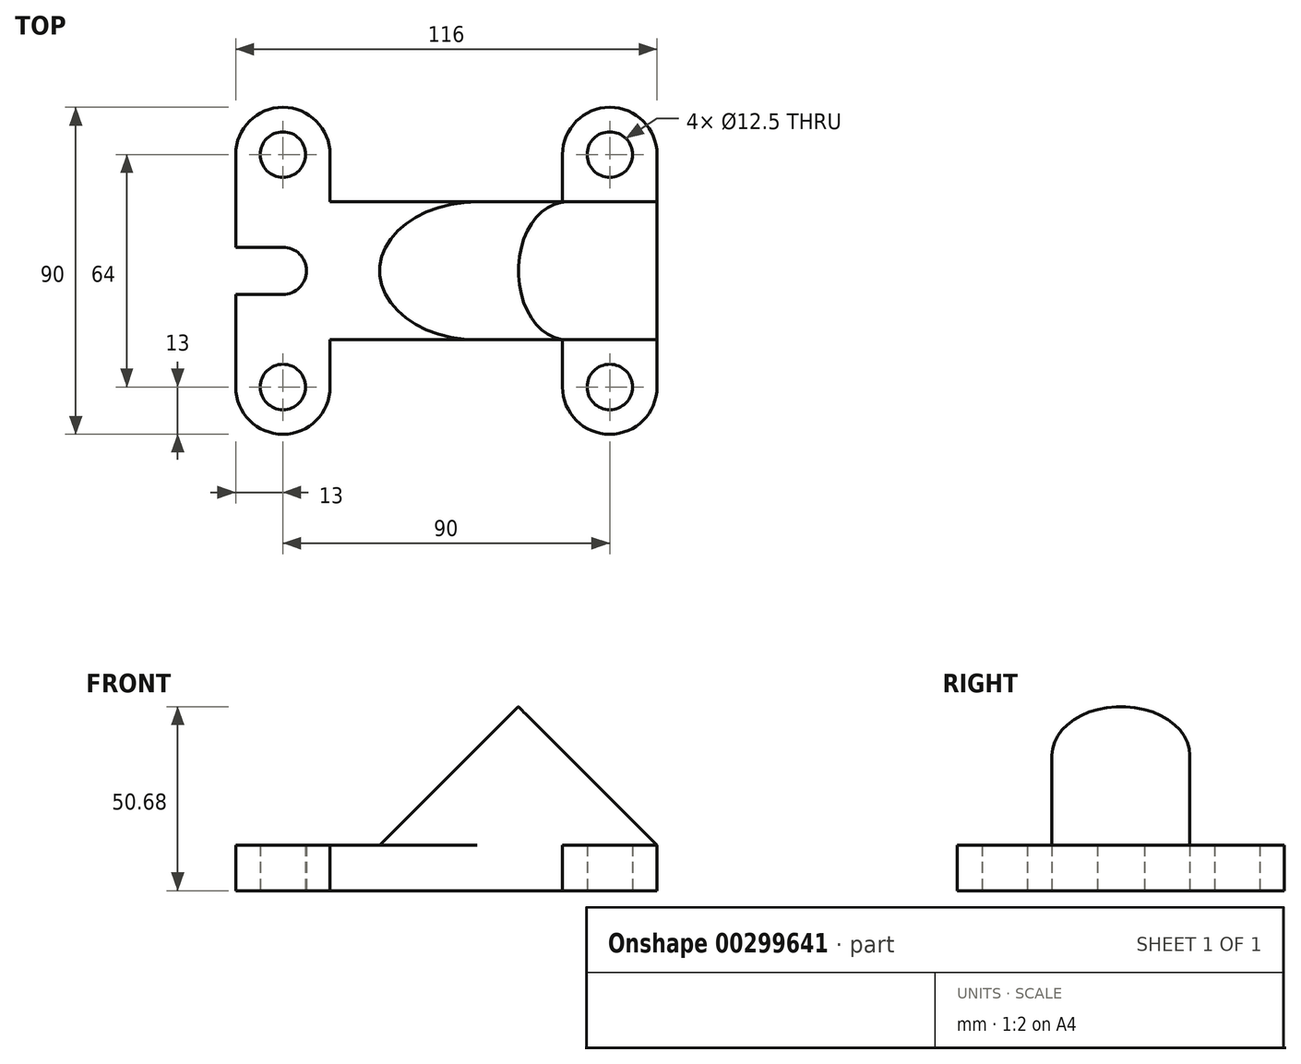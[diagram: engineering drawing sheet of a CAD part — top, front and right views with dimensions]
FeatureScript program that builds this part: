
annotation { "Feature Type Name" : "Feature", "Feature Type Description" : "" }
export const myFeature = defineFeature(function(context is Context, id is Id, definition is map)
    precondition{}
    {
        {
            var Q0;
            Q0=qCreatedBy(makeId("Top.planeOp"),FACE);
            var sketch = newSketch(context, id + "F0", { "sketchPlane" : qUnion([Q0])});
            skArc(sketch, "E0", {"start": v(-13, 0) * mm, "mid": v(0, -13) * mm, "end": v(13, 0) * mm});
            skArc(sketch, "E1.0.1.0", {"start": v(13, 64) * mm, "mid": v(0, 77) * mm, "end": v(-13, 64) * mm});
            skArc(sketch, "E1.1.0.0", {"start": v(77, 0) * mm, "mid": v(90, -13) * mm, "end": v(103, 0) * mm});
            skArc(sketch, "E1.1.1.0", {"start": v(103, 64) * mm, "mid": v(90, 77) * mm, "end": v(77, 64) * mm});
            skLineSegment(sketch, "E1.direction1", {"start": v(0, 0) * mm, "end": v(90, 0) * mm, "construction": true});
            skLineSegment(sketch, "E1.direction2", {"start": v(0, 0) * mm, "end": v(0, 64) * mm, "construction": true});
            skLineSegment(sketch, "E2", {"start": v(103, 0) * mm, "end": v(103, 64) * mm});
            skLineSegment(sketch, "E3", {"start": v(-13, 0) * mm, "end": v(-13, 25.5) * mm});
            skArc(sketch, "E4", {"start": v(0, 25.5) * mm, "mid": v(6.5, 32) * mm, "end": v(0, 38.5) * mm});
            skLineSegment(sketch, "E5", {"start": v(0, 38.5) * mm, "end": v(-13, 38.5) * mm});
            skLineSegment(sketch, "E6", {"start": v(0, 25.5) * mm, "end": v(-13, 25.5) * mm});
            skLineSegment(sketch, "E7", {"start": v(0, 32) * mm, "end": v(90, 32) * mm, "construction": true});
            skLineSegment(sketch, "E8.0", {"start": v(13, 13) * mm, "end": v(77, 13) * mm});
            skLineSegment(sketch, "E9.0", {"start": v(13, 51) * mm, "end": v(77, 51) * mm});
            skLineSegment(sketch, "E10", {"start": v(13, 64) * mm, "end": v(13, 51) * mm});
            skLineSegment(sketch, "E11", {"start": v(77, 64) * mm, "end": v(77, 51) * mm});
            skLineSegment(sketch, "E12", {"start": v(77, 0) * mm, "end": v(77, 13) * mm});
            skLineSegment(sketch, "E13", {"start": v(13, 0) * mm, "end": v(13, 13) * mm});
            skLineSegment(sketch, "E14.trimOffspring", {"start": v(-13, 38.5) * mm, "end": v(-13, 64) * mm});
            skCircle(sketch, "E15", {"center": v(0, 64) * mm, "radius": 6.25 * mm});
            skCircle(sketch, "E16", {"center": v(0, 0) * mm, "radius": 6.25 * mm});
            skCircle(sketch, "E17", {"center": v(90, 0) * mm, "radius": 6.25 * mm});
            skCircle(sketch, "E18", {"center": v(90, 64) * mm, "radius": 6.25 * mm});
            skSolve(sketch);
        }
        {
            var Q0;
            Q0=makeQuery(id+"F0.imprint","IMPRINT",FACE,{"disambiguationData":[TD([[makeQuery(id+"F0.imprint","IMPRINT",EDGE,{"derivedFrom":sQuery(id+"F0.wireOp",EDGE,"E0")}),1.0]])]});
            extrude(context, id + "F1", {"entities" : qUnion([Q0]), "depth" : 12.5 * mm});
        }
        {
            var Q0;
            Q0=makeQuery(id+"F1.opExtrude","SWEPT_FACE",FACE,{"disambiguationData":[OSD([sQuery(id+"F0.wireOp",EDGE,"E8.0")])]});
            var sketch = newSketch(context, id + "F2", { "sketchPlane" : qUnion([Q0])});
            skLineSegment(sketch, "E19.0", {"start": v(77, 12.5) * mm, "end": v(103, 12.5) * mm});
            skLineSegment(sketch, "E20", {"start": v(103, 12.5) * mm, "end": v(64.82, 50.68) * mm});
            skLineSegment(sketch, "E21", {"start": v(64.82, 50.68) * mm, "end": v(26.63, 12.5) * mm});
            skSolve(sketch);
        }
        {
            var Q0;
            {var subQ0=sQuery(id+"F2.wireOp",EDGE,"E19.0");Q0=makeQuery(id+"F2.imprint","IMPRINT",FACE,{"disambiguationData":[TD([[makeQuery(id+"F2.imprint","IMPRINT",EDGE,{"derivedFrom":subQ0}),1.0]])]});}
            extrude(context, id + "F3", {"entities" : qUnion([Q0]), "operationType" : NewBodyOperationType.ADD, "oppositeDirection" : true, "depth" : (19 * 2) * mm});
        }
        {
            var Q0;
            Q0=makeQuery(id+"F3.opExtrude","CAP_EDGE",EDGE,{"disambiguationData":[OSD([sQuery(id+"F2.wireOp",EDGE,"E21")])],"isStart":true});
            var Q1;
            Q1=makeQuery(id+"F3.opExtrude","CAP_EDGE",EDGE,{"disambiguationData":[OSD([sQuery(id+"F2.wireOp",EDGE,"E21")])],"isStart":false});
            fillet(context, id + "F4", {"entities" : qUnion([Q0, Q1]), "radius" : 19 * mm, "tangentPropagation" : true, "allowEdgeOverflow" : false});
        }
        {
            var Q0;
            Q0=makeQuery(id+"F3.opExtrude","SWEPT_FACE",FACE,{"disambiguationData":[OSD([sQuery(id+"F2.wireOp",EDGE,"E20")])]});
            var sketch = newSketch(context, id + "F5", { "sketchPlane" : qUnion([Q0])});
            skArc(sketch, "E22.0", {"start": v(29, 51) * mm, "mid": v(10, 32) * mm, "end": v(29, 13) * mm});
            skCircle(sketch, "E23", {"center": v(29, 32) * mm, "radius": 12.5 * mm, "construction": true});
            skCircle(sketch, "E24", {"center": v(16.5, 32) * mm, "radius": 2.5 * mm});
            skPoint(sketch, "E25.center", {"position": v(0, 0) * mm});
            skCircle(sketch, "E26.1.0", {"center": v(25.13, 20.11) * mm, "radius": 2.5 * mm});
            skCircle(sketch, "E26.2.0", {"center": v(39.1, 24.65) * mm, "radius": 2.5 * mm});
            skCircle(sketch, "E26.3.0", {"center": v(39.1, 39.35) * mm, "radius": 2.5 * mm});
            skCircle(sketch, "E26.4.0", {"center": v(25.13, 43.89) * mm, "radius": 2.5 * mm});
            skSolve(sketch);
        }
        {
            var Q0;
            Q0=makeQuery(id+"F5.imprint","IMPRINT",FACE,{"disambiguationData":[TD([[makeQuery(id+"F5.imprint","IMPRINT",EDGE,{"derivedFrom":sQuery(id+"F5.wireOp",EDGE,"E26.1.0")}),1.0]])]});
            var Q1;
            Q1=makeQuery(id+"F5.imprint","IMPRINT",FACE,{"disambiguationData":[TD([[makeQuery(id+"F5.imprint","IMPRINT",EDGE,{"derivedFrom":sQuery(id+"F5.wireOp",EDGE,"E26.2.0")}),1.0]])]});
            var Q2;
            Q2=makeQuery(id+"F5.imprint","IMPRINT",FACE,{"disambiguationData":[TD([[makeQuery(id+"F5.imprint","IMPRINT",EDGE,{"derivedFrom":sQuery(id+"F5.wireOp",EDGE,"E26.3.0")}),1.0]])]});
            var Q3;
            Q3=makeQuery(id+"F5.imprint","IMPRINT",FACE,{"disambiguationData":[TD([[makeQuery(id+"F5.imprint","IMPRINT",EDGE,{"derivedFrom":sQuery(id+"F5.wireOp",EDGE,"E26.4.0")}),1.0]])]});
            var Q4;
            Q4=makeQuery(id+"F5.imprint","IMPRINT",FACE,{"disambiguationData":[TD([[makeQuery(id+"F5.imprint","IMPRINT",EDGE,{"derivedFrom":sQuery(id+"F5.wireOp",EDGE,"E24")}),1.0]])]});
            extrude(context, id + "F6", {"entities" : qUnion([Q0, Q1, Q2, Q3, Q4]), "operationType" : NewBodyOperationType.REMOVE, "oppositeDirection" : true, "depth" : 5 * mm});
        }
        {
            var Q0;
            Q0=makeQuery(id+"F3.opExtrude","SWEPT_FACE",FACE,{"disambiguationData":[OSD([sQuery(id+"F2.wireOp",EDGE,"E20")])]});
            var sketch = newSketch(context, id + "F7", { "sketchPlane" : qUnion([Q0])});
            skArc(sketch, "E27.0", {"start": v(29, 51) * mm, "mid": v(10, 32) * mm, "end": v(29, 13) * mm});
            skCircle(sketch, "E28", {"center": v(29, 32) * mm, "radius": 7.5 * mm});
            skSolve(sketch);
        }
        {
            var Q0;
            Q0=makeQuery(id+"F7.imprint","IMPRINT",FACE,{"disambiguationData":[TD([[makeQuery(id+"F7.imprint","IMPRINT",EDGE,{"derivedFrom":sQuery(id+"F7.wireOp",EDGE,"E28")}),1.0]])]});
            extrude(context, id + "F8", {"entities" : qUnion([Q0]), "operationType" : NewBodyOperationType.REMOVE, "oppositeDirection" : true, "depth" : 100 * mm});
        }
    });
